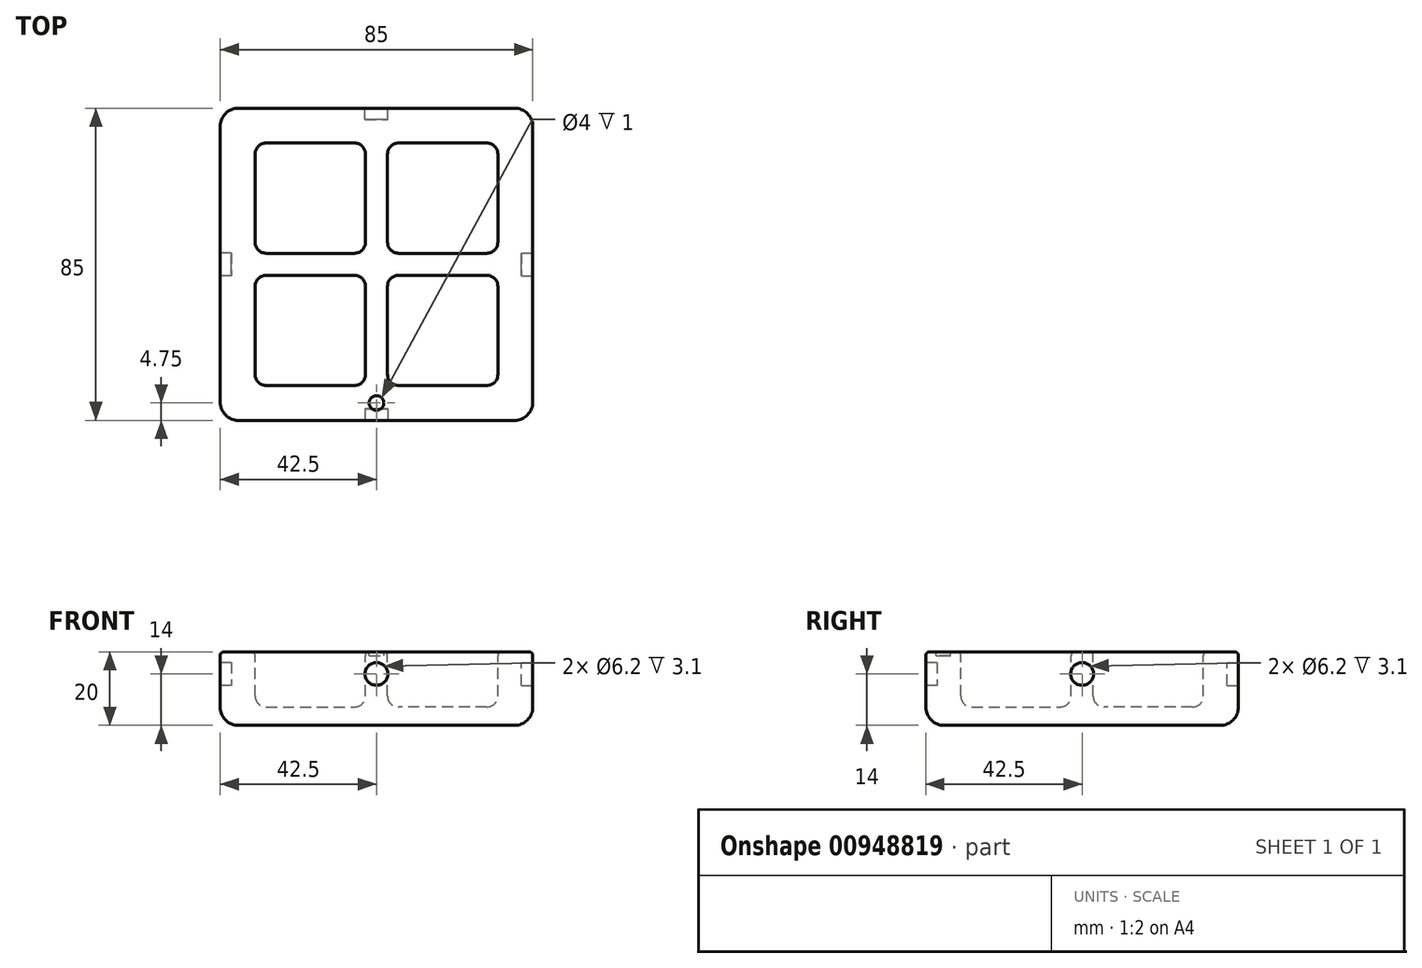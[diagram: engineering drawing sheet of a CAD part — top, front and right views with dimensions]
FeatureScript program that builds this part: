
annotation { "Feature Type Name" : "Feature", "Feature Type Description" : "" }
export const myFeature = defineFeature(function(context is Context, id is Id, definition is map)
    precondition{}
    {
        {
            var Q0;
            Q0=qCreatedBy(makeId("Top.planeOp"),FACE);
            var sketch = newSketch(context, id + "F0", { "sketchPlane" : qUnion([Q0])});
            skLineSegment(sketch, "E0.bottom", {"start": v(-42.5, 42.5) * mm, "end": v(42.5, 42.5) * mm});
            skLineSegment(sketch, "E0.top", {"start": v(-42.5, -42.5) * mm, "end": v(42.5, -42.5) * mm});
            skLineSegment(sketch, "E0.left", {"start": v(-42.5, 42.5) * mm, "end": v(-42.5, -42.5) * mm});
            skLineSegment(sketch, "E0.right", {"start": v(42.5, 42.5) * mm, "end": v(42.5, -42.5) * mm});
            skLineSegment(sketch, "E1.bottom", {"start": v(-30, 33) * mm, "end": v(-6, 33) * mm});
            skLineSegment(sketch, "E1.top", {"start": v(-30, 3) * mm, "end": v(-6, 3) * mm});
            skLineSegment(sketch, "E1.left", {"start": v(-33, 30) * mm, "end": v(-33, 6) * mm});
            skLineSegment(sketch, "E1.right", {"start": v(-3, 30) * mm, "end": v(-3, 6) * mm});
            skLineSegment(sketch, "E2.direction1", {"start": v(-33, 3) * mm, "end": v(-8.24, 3) * mm, "construction": true});
            skPoint(sketch, "E3.visualSharp", {"position": v(-33, 33) * mm});
            skArc(sketch, "E3.filletArc", {"start": v(-30, 33) * mm, "mid": v(-32.12, 32.12) * mm, "end": v(-33, 30) * mm});
            skPoint(sketch, "E4.visualSharp", {"position": v(-3, 33) * mm});
            skArc(sketch, "E4.filletArc", {"start": v(-3, 30) * mm, "mid": v(-3.88, 32.12) * mm, "end": v(-6, 33) * mm});
            skPoint(sketch, "E5.visualSharp", {"position": v(-3, 3) * mm});
            skArc(sketch, "E5.filletArc", {"start": v(-6, 3) * mm, "mid": v(-3.88, 3.88) * mm, "end": v(-3, 6) * mm});
            skPoint(sketch, "E6.visualSharp", {"position": v(-33, 3) * mm});
            skArc(sketch, "E6.filletArc", {"start": v(-33, 6) * mm, "mid": v(-32.12, 3.88) * mm, "end": v(-30, 3) * mm});
            skLineSegment(sketch, "E7.direction1", {"start": v(-33, 3) * mm, "end": v(-6.5, 3) * mm, "construction": true});
            skLineSegment(sketch, "E8", {"start": v(-42.5, 0) * mm, "end": v(42.5, 0) * mm, "construction": true});
            skLineSegment(sketch, "E9", {"start": v(0, -42.5) * mm, "end": v(0, 42.5) * mm, "construction": true});
            skCircle(sketch, "E10", {"center": v(0, -37.75) * mm, "radius": 2 * mm});
            skLineSegment(sketch, "E11.MirrorCS", {"start": v(33, 30) * mm, "end": v(33, 6) * mm});
            skArc(sketch, "E12.MirrorCS", {"start": v(30, 33) * mm, "mid": v(32.12, 32.12) * mm, "end": v(33, 30) * mm});
            skLineSegment(sketch, "E13.MirrorCS", {"start": v(30, 33) * mm, "end": v(6, 33) * mm});
            skArc(sketch, "E14.MirrorCS", {"start": v(3, 30) * mm, "mid": v(3.88, 32.12) * mm, "end": v(6, 33) * mm});
            skLineSegment(sketch, "E15.MirrorCS", {"start": v(3, 30) * mm, "end": v(3, 6) * mm});
            skPoint(sketch, "E16.MirrorP", {"position": v(3, 3) * mm});
            skArc(sketch, "E17.MirrorCS", {"start": v(6, 3) * mm, "mid": v(3.88, 3.88) * mm, "end": v(3, 6) * mm});
            skLineSegment(sketch, "E18.MirrorCS", {"start": v(30, 3) * mm, "end": v(6, 3) * mm});
            skArc(sketch, "E19.MirrorCS", {"start": v(33, 6) * mm, "mid": v(32.12, 3.88) * mm, "end": v(30, 3) * mm});
            skLineSegment(sketch, "E20.MirrorCS", {"start": v(-30, -3) * mm, "end": v(-6, -3) * mm});
            skLineSegment(sketch, "E21.MirrorCS", {"start": v(-30, -33) * mm, "end": v(-6, -33) * mm});
            skLineSegment(sketch, "E22.MirrorCS", {"start": v(-3, -30) * mm, "end": v(-3, -6) * mm});
            skLineSegment(sketch, "E23.MirrorCS", {"start": v(-33, -30) * mm, "end": v(-33, -6) * mm});
            skArc(sketch, "E24.MirrorCS", {"start": v(-33, -6) * mm, "mid": v(-32.12, -3.88) * mm, "end": v(-30, -3) * mm});
            skArc(sketch, "E25.MirrorCS", {"start": v(-6, -3) * mm, "mid": v(-3.88, -3.88) * mm, "end": v(-3, -6) * mm});
            skArc(sketch, "E26.MirrorCS", {"start": v(-3, -30) * mm, "mid": v(-3.88, -32.12) * mm, "end": v(-6, -33) * mm});
            skArc(sketch, "E27.MirrorCS", {"start": v(-30, -33) * mm, "mid": v(-32.12, -32.12) * mm, "end": v(-33, -30) * mm});
            skLineSegment(sketch, "E28.MirrorCS", {"start": v(30, -3) * mm, "end": v(6, -3) * mm});
            skArc(sketch, "E29.MirrorCS", {"start": v(6, -3) * mm, "mid": v(3.88, -3.88) * mm, "end": v(3, -6) * mm});
            skLineSegment(sketch, "E30.MirrorCS", {"start": v(3, -30) * mm, "end": v(3, -6) * mm});
            skArc(sketch, "E31.MirrorCS", {"start": v(3, -30) * mm, "mid": v(3.88, -32.12) * mm, "end": v(6, -33) * mm});
            skArc(sketch, "E32.MirrorCS", {"start": v(30, -33) * mm, "mid": v(32.12, -32.12) * mm, "end": v(33, -30) * mm});
            skLineSegment(sketch, "E33.MirrorCS", {"start": v(33, -30) * mm, "end": v(33, -6) * mm});
            skArc(sketch, "E34.MirrorCS", {"start": v(33, -6) * mm, "mid": v(32.12, -3.88) * mm, "end": v(30, -3) * mm});
            skLineSegment(sketch, "E35.MirrorCS", {"start": v(30, -33) * mm, "end": v(6, -33) * mm});
            skSolve(sketch);
        }
        {
            var Q0;
            Q0=makeQuery(id+"F0.imprint","IMPRINT",FACE,{"disambiguationData":[TD([[makeQuery(id+"F0.imprint","IMPRINT",EDGE,{"derivedFrom":sQuery(id+"F0.wireOp",EDGE,"E1.bottom")}),-1.0]])]});
            var Q1;
            Q1=makeQuery(id+"F0.imprint","IMPRINT",FACE,{"disambiguationData":[TD([[makeQuery(id+"F0.imprint","IMPRINT",EDGE,{"derivedFrom":sQuery(id+"F0.wireOp",EDGE,"E0.bottom")}),-1.0]])]});
            var Q2;
            Q2=makeQuery(id+"F0.imprint","IMPRINT",FACE,{"disambiguationData":[TD([[makeQuery(id+"F0.imprint","IMPRINT",EDGE,{"derivedFrom":sQuery(id+"F0.wireOp",EDGE,"E10")}),1.0]])]});
            var Q3;
            Q3=makeQuery(id+"F0.imprint","IMPRINT",FACE,{"disambiguationData":[TD([[makeQuery(id+"F0.imprint","IMPRINT",EDGE,{"derivedFrom":sQuery(id+"F0.wireOp",EDGE,"E11.MirrorCS")}),-1.0]])]});
            var Q4;
            Q4=makeQuery(id+"F0.imprint","IMPRINT",FACE,{"disambiguationData":[TD([[makeQuery(id+"F0.imprint","IMPRINT",EDGE,{"derivedFrom":sQuery(id+"F0.wireOp",EDGE,"E28.MirrorCS")}),1.0]])]});
            var Q5;
            Q5=makeQuery(id+"F0.imprint","IMPRINT",FACE,{"disambiguationData":[TD([[makeQuery(id+"F0.imprint","IMPRINT",EDGE,{"derivedFrom":sQuery(id+"F0.wireOp",EDGE,"E20.MirrorCS")}),-1.0]])]});
            extrude(context, id + "F1", {"entities" : qUnion([Q0, Q1, Q2, Q3, Q4, Q5]), "depth" : 20 * mm, "offsetDistance" : 25 * mm});
        }
        {
            var Q0;
            Q0=makeQuery(id+"F0.imprint","IMPRINT",FACE,{"disambiguationData":[TD([[makeQuery(id+"F0.imprint","IMPRINT",EDGE,{"derivedFrom":sQuery(id+"F0.wireOp",EDGE,"E1.bottom")}),-1.0]])]});
            var Q1;
            Q1=makeQuery(id+"F0.imprint","IMPRINT",FACE,{"disambiguationData":[TD([[makeQuery(id+"F0.imprint","IMPRINT",EDGE,{"derivedFrom":sQuery(id+"F0.wireOp",EDGE,"E20.MirrorCS")}),-1.0]])]});
            var Q2;
            Q2=makeQuery(id+"F0.imprint","IMPRINT",FACE,{"disambiguationData":[TD([[makeQuery(id+"F0.imprint","IMPRINT",EDGE,{"derivedFrom":sQuery(id+"F0.wireOp",EDGE,"E28.MirrorCS")}),1.0]])]});
            var Q3;
            Q3=makeQuery(id+"F0.imprint","IMPRINT",FACE,{"disambiguationData":[TD([[makeQuery(id+"F0.imprint","IMPRINT",EDGE,{"derivedFrom":sQuery(id+"F0.wireOp",EDGE,"E11.MirrorCS")}),-1.0]])]});
            extrude(context, id + "F2", {"entities" : qUnion([Q0, Q1, Q2, Q3]), "operationType" : NewBodyOperationType.REMOVE, "depth" : 15 * mm, "offsetDistance" : 25 * mm});
        }
        {
            var Q0;
            Q0=makeQuery(id+"F1.opExtrude","CAP_FACE",FACE,{"disambiguationData":[OSD([sQuery(id+"F0.wireOp",EDGE,"E0.bottom"),sQuery(id+"F0.wireOp",EDGE,"E0.top"),sQuery(id+"F0.wireOp",EDGE,"E0.left"),sQuery(id+"F0.wireOp",EDGE,"E0.right")])],"isStart":false});
            var Q1;
            Q1=makeQuery(id+"F1.opExtrude","SWEPT_EDGE",EDGE,{"disambiguationData":[OSD([sQuery(id+"F0.wireOp",EDGE,"E0.bottom"),sQuery(id+"F0.wireOp",EDGE,"E0.right")])]});
            var Q2;
            Q2=makeQuery(id+"F1.opExtrude","SWEPT_EDGE",EDGE,{"disambiguationData":[OSD([sQuery(id+"F0.wireOp",EDGE,"E0.bottom"),sQuery(id+"F0.wireOp",EDGE,"E0.left")])]});
            var Q3;
            Q3=makeQuery(id+"F1.opExtrude","SWEPT_EDGE",EDGE,{"disambiguationData":[OSD([sQuery(id+"F0.wireOp",EDGE,"E0.top"),sQuery(id+"F0.wireOp",EDGE,"E0.left")])]});
            var Q4;
            Q4=makeQuery(id+"F1.opExtrude","SWEPT_EDGE",EDGE,{"disambiguationData":[OSD([sQuery(id+"F0.wireOp",EDGE,"E0.top"),sQuery(id+"F0.wireOp",EDGE,"E0.right")])]});
            fillet(context, id + "F3", {"entities" : qUnion([Q0, Q1, Q2, Q3, Q4]), "radius" : 5 * mm, "tangentPropagation" : true, "allowEdgeOverflow" : false});
        }
        {
            var Q0;
            Q0=makeQuery(id+"F2.boolean.opBoolean","COPY",FACE,{"derivedFrom":makeQuery(id+"F2.opExtrude","CAP_FACE",FACE,{"disambiguationData":[OSD([sQuery(id+"F0.wireOp",EDGE,"E1.bottom"),sQuery(id+"F0.wireOp",EDGE,"E1.top"),sQuery(id+"F0.wireOp",EDGE,"E1.left"),sQuery(id+"F0.wireOp",EDGE,"E1.right"),sQuery(id+"F0.wireOp",EDGE,"E3.filletArc"),sQuery(id+"F0.wireOp",EDGE,"E4.filletArc"),sQuery(id+"F0.wireOp",EDGE,"E5.filletArc"),sQuery(id+"F0.wireOp",EDGE,"E6.filletArc")])],"isStart":false})});
            var Q1;
            Q1=makeQuery(id+"F2.boolean.opBoolean","COPY",FACE,{"derivedFrom":makeQuery(id+"F2.opExtrude","CAP_FACE",FACE,{"disambiguationData":[OSD([sQuery(id+"F0.wireOp",EDGE,"E20.MirrorCS"),sQuery(id+"F0.wireOp",EDGE,"E21.MirrorCS"),sQuery(id+"F0.wireOp",EDGE,"E22.MirrorCS"),sQuery(id+"F0.wireOp",EDGE,"E23.MirrorCS"),sQuery(id+"F0.wireOp",EDGE,"E24.MirrorCS"),sQuery(id+"F0.wireOp",EDGE,"E25.MirrorCS"),sQuery(id+"F0.wireOp",EDGE,"E26.MirrorCS"),sQuery(id+"F0.wireOp",EDGE,"E27.MirrorCS")])],"isStart":false})});
            var Q2;
            Q2=makeQuery(id+"F2.boolean.opBoolean","COPY",FACE,{"derivedFrom":makeQuery(id+"F2.opExtrude","CAP_FACE",FACE,{"disambiguationData":[OSD([sQuery(id+"F0.wireOp",EDGE,"E28.MirrorCS"),sQuery(id+"F0.wireOp",EDGE,"E29.MirrorCS"),sQuery(id+"F0.wireOp",EDGE,"E30.MirrorCS"),sQuery(id+"F0.wireOp",EDGE,"E31.MirrorCS"),sQuery(id+"F0.wireOp",EDGE,"E32.MirrorCS"),sQuery(id+"F0.wireOp",EDGE,"E33.MirrorCS"),sQuery(id+"F0.wireOp",EDGE,"E34.MirrorCS"),sQuery(id+"F0.wireOp",EDGE,"E35.MirrorCS")])],"isStart":false})});
            var Q3;
            Q3=makeQuery(id+"F2.boolean.opBoolean","COPY",FACE,{"derivedFrom":makeQuery(id+"F2.opExtrude","CAP_FACE",FACE,{"disambiguationData":[OSD([sQuery(id+"F0.wireOp",EDGE,"E11.MirrorCS"),sQuery(id+"F0.wireOp",EDGE,"E12.MirrorCS"),sQuery(id+"F0.wireOp",EDGE,"E13.MirrorCS"),sQuery(id+"F0.wireOp",EDGE,"E14.MirrorCS"),sQuery(id+"F0.wireOp",EDGE,"E15.MirrorCS"),sQuery(id+"F0.wireOp",EDGE,"E17.MirrorCS"),sQuery(id+"F0.wireOp",EDGE,"E18.MirrorCS"),sQuery(id+"F0.wireOp",EDGE,"E19.MirrorCS")])],"isStart":false})});
            fillet(context, id + "F4", {"entities" : qUnion([Q0, Q1, Q2, Q3]), "radius" : 3 * mm, "tangentPropagation" : true, "allowEdgeOverflow" : false});
        }
        {
            var Q0;
            Q0=makeQuery(id+"F1.opExtrude","CAP_FACE",FACE,{"disambiguationData":[OSD([sQuery(id+"F0.wireOp",EDGE,"E0.bottom"),sQuery(id+"F0.wireOp",EDGE,"E0.top"),sQuery(id+"F0.wireOp",EDGE,"E0.left"),sQuery(id+"F0.wireOp",EDGE,"E0.right")])],"isStart":true});
            fillet(context, id + "F5", {"entities" : qUnion([Q0]), "radius" : 1 * mm, "tangentPropagation" : true, "allowEdgeOverflow" : false});
        }
        {
            var Q0;
            Q0=makeQuery(id+"F1.opExtrude","SWEPT_FACE",FACE,{"disambiguationData":[OSD([sQuery(id+"F0.wireOp",EDGE,"E0.top")])]});
            var sketch = newSketch(context, id + "F6", { "sketchPlane" : qUnion([Q0])});
            skCircle(sketch, "E36", {"center": v(0, 6) * mm, "radius": 3.1 * mm});
            skSolve(sketch);
        }
        {
            var Q0;
            Q0=makeQuery(id+"F6.imprint","IMPRINT",FACE,{"disambiguationData":[TD([[makeQuery(id+"F6.imprint","IMPRINT",EDGE,{"derivedFrom":sQuery(id+"F6.wireOp",EDGE,"E36")}),1.0]])]});
            extrude(context, id + "F7", {"entities" : qUnion([Q0]), "operationType" : NewBodyOperationType.REMOVE, "oppositeDirection" : true, "depth" : 3.1 * mm, "offsetDistance" : 25 * mm});
        }
        {
            var Q0;
            Q0=makeQuery(id+"F1.opExtrude","SWEPT_FACE",FACE,{"disambiguationData":[OSD([sQuery(id+"F0.wireOp",EDGE,"E0.bottom")])]});
            var sketch = newSketch(context, id + "F8", { "sketchPlane" : qUnion([Q0])});
            skCircle(sketch, "E37", {"center": v(0, 6) * mm, "radius": 3.1 * mm});
            skSolve(sketch);
        }
        {
            var Q0;
            Q0=makeQuery(id+"F8.imprint","IMPRINT",FACE,{"disambiguationData":[TD([[makeQuery(id+"F8.imprint","IMPRINT",EDGE,{"derivedFrom":sQuery(id+"F8.wireOp",EDGE,"E37")}),1.0]])]});
            extrude(context, id + "F9", {"entities" : qUnion([Q0]), "operationType" : NewBodyOperationType.REMOVE, "oppositeDirection" : true, "depth" : 3.1 * mm, "offsetDistance" : 25 * mm});
        }
        {
            var Q0;
            Q0=makeQuery(id+"F1.opExtrude","SWEPT_FACE",FACE,{"disambiguationData":[OSD([sQuery(id+"F0.wireOp",EDGE,"E0.left")])]});
            var sketch = newSketch(context, id + "F10", { "sketchPlane" : qUnion([Q0])});
            skCircle(sketch, "E38", {"center": v(0, 6) * mm, "radius": 3.1 * mm});
            skSolve(sketch);
        }
        {
            var Q0;
            Q0=makeQuery(id+"F10.imprint","IMPRINT",FACE,{"disambiguationData":[TD([[makeQuery(id+"F10.imprint","IMPRINT",EDGE,{"derivedFrom":sQuery(id+"F10.wireOp",EDGE,"E38")}),1.0]])]});
            extrude(context, id + "F11", {"entities" : qUnion([Q0]), "operationType" : NewBodyOperationType.REMOVE, "oppositeDirection" : true, "depth" : 3.1 * mm, "offsetDistance" : 25 * mm});
        }
        {
            var Q0;
            Q0=makeQuery(id+"F1.opExtrude","SWEPT_FACE",FACE,{"disambiguationData":[OSD([sQuery(id+"F0.wireOp",EDGE,"E0.right")])]});
            var sketch = newSketch(context, id + "F12", { "sketchPlane" : qUnion([Q0])});
            skCircle(sketch, "E39", {"center": v(0, 6) * mm, "radius": 3.1 * mm});
            skSolve(sketch);
        }
        {
            var Q0;
            Q0=makeQuery(id+"F12.imprint","IMPRINT",FACE,{"disambiguationData":[TD([[makeQuery(id+"F12.imprint","IMPRINT",EDGE,{"derivedFrom":sQuery(id+"F12.wireOp",EDGE,"E39")}),1.0]])]});
            extrude(context, id + "F13", {"entities" : qUnion([Q0]), "operationType" : NewBodyOperationType.REMOVE, "oppositeDirection" : true, "depth" : 3.1 * mm, "offsetDistance" : 25 * mm});
        }
        {
            var Q0;
            Q0=makeQuery(id+"F0.imprint","IMPRINT",FACE,{"disambiguationData":[TD([[makeQuery(id+"F0.imprint","IMPRINT",EDGE,{"derivedFrom":sQuery(id+"F0.wireOp",EDGE,"E10")}),1.0]])]});
            var Q1;
            Q1=sQuery(id+"F0.wireOp",EDGE,"E10");
            extrude(context, id + "F14", {"entities" : qUnion([Q0]), "operationType" : NewBodyOperationType.REMOVE, "surfaceEntities" : qUnion([Q1]), "depth" : 1 * mm, "offsetDistance" : 25 * mm});
        }
        {
            var Q0;
            Q0=makeQuery(id+"F1.opExtrude","SWEPT_BODY",BODY,{"disambiguationData":[OSD([sQuery(id+"F0.wireOp",EDGE,"E0.bottom"),sQuery(id+"F0.wireOp",EDGE,"E0.top"),sQuery(id+"F0.wireOp",EDGE,"E0.left"),sQuery(id+"F0.wireOp",EDGE,"E0.right")])]});
            var Q1;
            Q1=sQuery(id+"F0.wireOp",EDGE,"E9");
            transform(context, id + "F15", {"entities" : qUnion([Q0]), "transformType" : TransformType.ROTATION, "transformAxis" : qUnion([Q1]), "angle" : 180 * degree, "makeCopy" : false});
        }
    });
